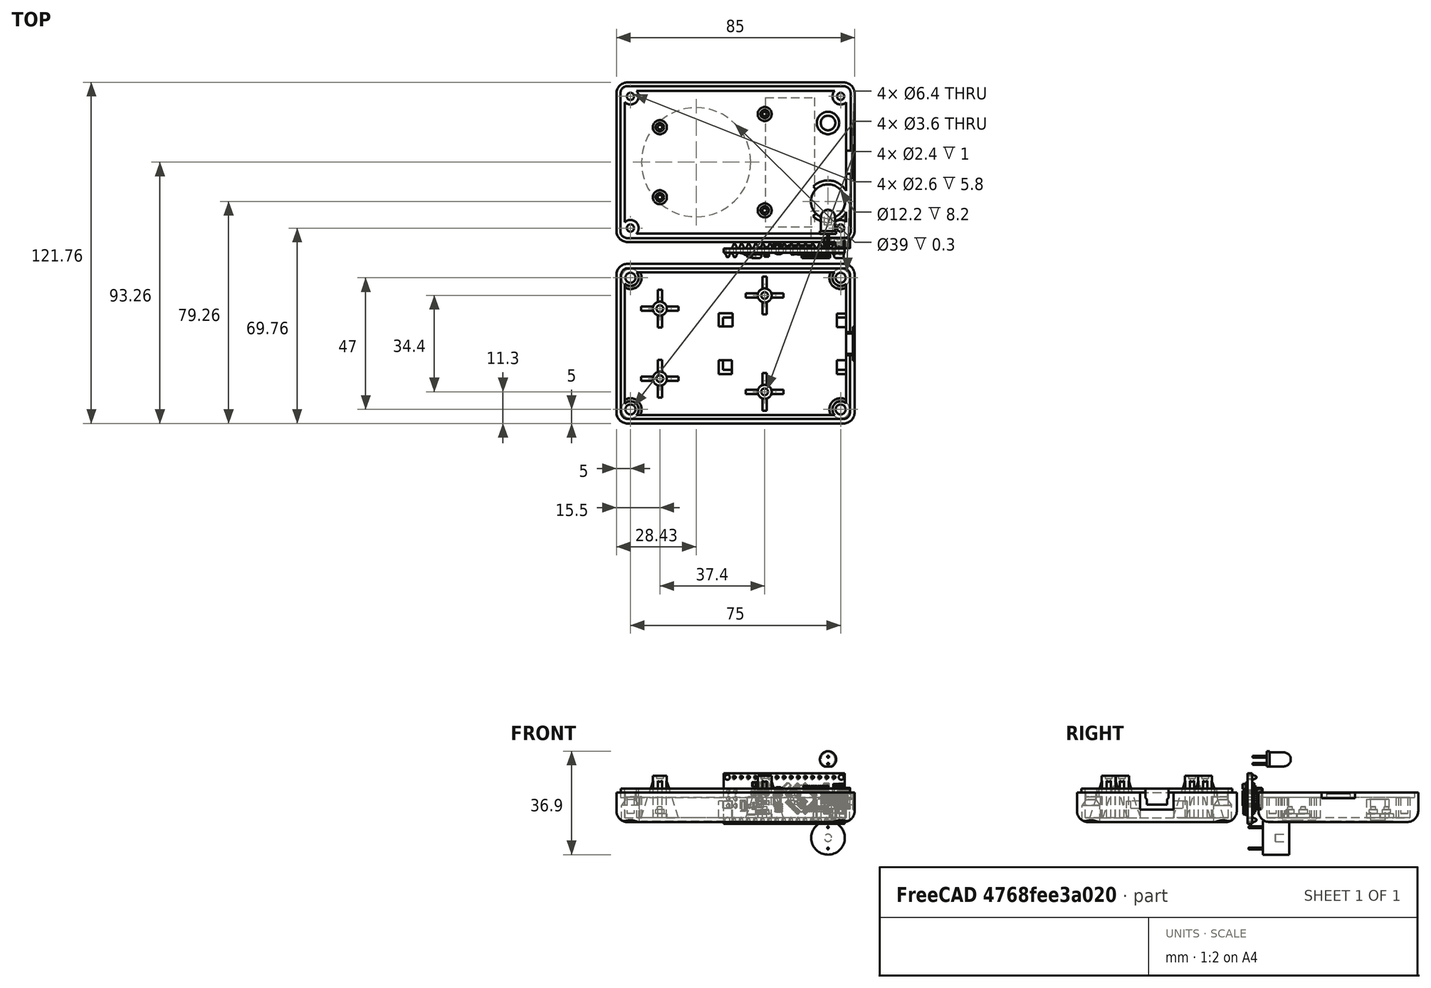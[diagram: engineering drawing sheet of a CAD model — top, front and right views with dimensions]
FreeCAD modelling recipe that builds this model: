
FCSTD DOCUMENT  (FreeCAD 0.17R13541 (Git))
Label: sportduino-master
License: All rights reserved
LicenseURL: http://en.wikipedia.org/wiki/All_rights_reserved
objects: Part::Feature×51, Part::MultiFuse×33, Part::Cylinder×24, Part::Cut×24, Part::FeaturePython×24, Part::Box×20, Part::Fillet×3, App::DocumentObjectGroup×1, Part::Sphere×1, Mesh::Feature×1, Part::Extrusion×1, Part::Cone×1
note: 182 computed .brp shape members not serialized (recipe doc carries the construction recipe); baked Part::Feature solids carry a one-line shape summary decoded from their .brp

FEATURE [Part::Feature] Part__Feature  label="User Library-arduino_nano"
  shape: bbox 43.59 x 4.635 x 18 mm, 378 faces (baked)
FEATURE [Part::Feature] Part__Feature006  label="User Library-arduino_nano006"
  Placement = pos=(23.85,1.75,-7.62) rot=(0,1,0;3.92699rad)
  shape: bbox 11.22 x 1.101 x 11.22 mm, 1866 faces (baked)
FEATURE [Part::Feature] Part__Feature007  label="User Library-arduino_nano007"
  Placement = pos=(29.05,0,-7.67) rot=(0.707107,0,-0.707107;3.14159rad)
  shape: bbox 10.2 x 1.9 x 9.71 mm, 717 faces (baked)
FEATURE [Part::Feature] Part__Feature008  label="User Library-arduino_nano008"
  Placement = pos=(21.86,0,-5.8) rot=(0.707107,0,-0.707107;3.14159rad)
  shape: bbox 3.8 x 0.6006 x 1.7 mm, 74 faces (baked)
FEATURE [Part::Feature] Part__Feature009  label="User Library-arduino_nano009"
  Placement = pos=(21.86,0,-9) rot=(0.707107,0,-0.707107;3.14159rad)
  shape: bbox 3.8 x 0.6006 x 1.7 mm, 74 faces (baked)
FEATURE [Part::Feature] Part__Feature010  label="User Library-arduino_nano010"
  Placement = pos=(36.75,0,-7.6) rot=(0.707107,0,-0.707107;3.14159rad)
  shape: bbox 3.8 x 0.6006 x 1.7 mm, 74 faces (baked)
FEATURE [Part::Feature] Part__Feature011  label="User Library-arduino_nano011"
  Placement = pos=(36.75,0,-12) rot=(0.707107,0,-0.707107;3.14159rad)
  shape: bbox 3.8 x 0.6006 x 1.7 mm, 74 faces (baked)
FEATURE [Part::Feature] Part__Feature012  label="User Library-arduino_nano012"
  Placement = pos=(8.2,0,-2.6) rot=(0.707107,0,-0.707107;3.14159rad)
  shape: bbox 3.8 x 0.6006 x 1.7 mm, 74 faces (baked)
FEATURE [Part::Feature] Part__Feature013  label="User Library-arduino_nano013"
  Placement = pos=(10.4,1.6,-2.8) rot=(0,0,1;0rad)
  shape: bbox 5.556 x 0.5822 x 2.158 mm, 43 faces (baked)
FEATURE [Part::Feature] Part__Feature014  label="User Library-arduino_nano014"
  Placement = pos=(10.4,1.6,-2.8) rot=(0,0,1;0rad)
  shape: bbox 1.4 x 0.5 x 1.2 mm, 6 faces (baked)
FEATURE [Part::Feature] Part__Feature015  label="User Library-arduino_nano015"
  Placement = pos=(10.4,1.6,-5.55) rot=(0,0,1;0rad)
  shape: bbox 5.556 x 0.5822 x 2.158 mm, 43 faces (baked)
FEATURE [Part::Feature] Part__Feature016  label="User Library-arduino_nano016"
  Placement = pos=(10.4,1.6,-5.55) rot=(0,0,1;0rad)
  shape: bbox 1.4 x 0.5 x 1.2 mm, 6 faces (baked)
FEATURE [Part::Feature] Part__Feature017  label="User Library-arduino_nano017"
  Placement = pos=(10.4,1.6,-12.5) rot=(0,0,1;0rad)
  shape: bbox 5.556 x 0.5822 x 2.158 mm, 43 faces (baked)
FEATURE [Part::Feature] Part__Feature018  label="User Library-arduino_nano018"
  Placement = pos=(10.4,1.6,-12.5) rot=(0,0,1;0rad)
  shape: bbox 1.4 x 0.5 x 1.2 mm, 6 faces (baked)
FEATURE [Part::Feature] Part__Feature019  label="User Library-arduino_nano019"
  Placement = pos=(10.4,1.6,-9.05) rot=(0,0,1;0rad)
  shape: bbox 5.556 x 0.5822 x 2.158 mm, 43 faces (baked)
FEATURE [Part::Feature] Part__Feature020  label="User Library-arduino_nano020"
  Placement = pos=(10.4,1.6,-9.05) rot=(0,0,1;0rad)
  shape: bbox 1.4 x 0.5 x 1.2 mm, 6 faces (baked)
FEATURE [Part::Feature] Part__Feature021  label="User Library-arduino_nano021"
  Placement = pos=(18.5113,1.6,-3.55414) rot=(0,-1,0;0.785398rad)
  shape: bbox 3.584 x 0.8006 x 3.584 mm, 71 faces (baked)
FEATURE [Part::Feature] Part__Feature022  label="User Library-arduino_nano022"
  Placement = pos=(38.98,1.65,-7.62) rot=(0,-1,0;1.5708rad)
  shape: bbox 9.476 x 3.823 x 11.03 mm, 248 faces (baked)
FEATURE [Part::Feature] Part__Feature023  label="User Library-arduino_nano023"
  Placement = pos=(32.28,1.65,-7.62) rot=(0,1,0;1.5708rad)
  shape: bbox 8.2 x 4.5 x 7.7 mm, 127 faces (baked)
FEATURE [Part::Feature] Part__Feature024  label="User Library-arduino_nano024"
  Placement = pos=(33.28,1.65,-9.22) rot=(0,1,0;1.5708rad)
  shape: bbox 9.423 x 2.551 x 0.5011 mm, 31 faces (baked)
FEATURE [Part::Feature] Part__Feature025  label="User Library-arduino_nano025"
  Placement = pos=(33.28,1.65,-8.42) rot=(0,1,0;1.5708rad)
  shape: bbox 9.423 x 2.551 x 0.5011 mm, 31 faces (baked)
FEATURE [Part::Feature] Part__Feature026  label="User Library-arduino_nano026"
  Placement = pos=(33.28,1.65,-7.62) rot=(0,1,0;1.5708rad)
  shape: bbox 9.423 x 2.551 x 0.5011 mm, 31 faces (baked)
FEATURE [Part::Feature] Part__Feature027  label="User Library-arduino_nano027"
  Placement = pos=(33.28,1.65,-6.82) rot=(0,1,0;1.5708rad)
  shape: bbox 9.423 x 2.551 x 0.5011 mm, 31 faces (baked)
FEATURE [Part::Feature] Part__Feature028  label="User Library-arduino_nano028"
  Placement = pos=(33.28,1.65,-6.02) rot=(0,1,0;1.5708rad)
  shape: bbox 9.423 x 2.551 x 0.5011 mm, 31 faces (baked)
FEATURE [Part::Feature] Part__Feature029  label="User Library-arduino_nano029"
  Placement = pos=(37.2,0,-3.3) rot=(0.707107,0,0.707107;3.14159rad)
  shape: bbox 4 x 1.81 x 1.7 mm, 125 faces (baked)
FEATURE [Part::Feature] Part__Feature030  label="User Library-arduino_nano030"
  Placement = pos=(7.9,0,-5.6) rot=(0.707107,0,-0.707107;3.14159rad)
  shape: bbox 4 x 1.81 x 1.7 mm, 125 faces (baked)
FEATURE [Part::Feature] Part__Feature031  label="User Library-arduino_nano031"
  Placement = pos=(15.25,1.6,-8.05) rot=(0,1,0;1.5708rad)
  shape: bbox 2.8 x 2.156 x 5.2 mm, 77 faces (baked)
FEATURE [Part::Feature] Part__Feature032  label="User Library-arduino_nano032"
  Placement = pos=(15.25,3.25,-8.05) rot=(0,0,1;0rad)
  shape: bbox 3 x 1.65 x 4 mm, 72 faces (baked)
FEATURE [Part::Feature] Part__Feature033  label="User Library-arduino_nano033"
  Placement = pos=(6.1,0,-10.16) rot=(0.707107,0,-0.707107;3.14159rad)
  shape: bbox 8.3 x 1.689 x 6.5 mm, 197 faces (baked)
FEATURE [Part::Feature] Part__Feature034  label="User Library-arduino_nano034"
  Placement = pos=(11.43,0,-4.2) rot=(0.707107,0,0.707107;3.14159rad)
  shape: bbox 1.701 x 1.385 x 4.916 mm, 85 faces (baked)
FEATURE [Part::Feature] Part__Feature035  label="User Library-arduino_nano035"
  Placement = pos=(15.75,0,-10.85) rot=(0.707107,0,0.707107;3.14159rad)
  shape: bbox 1.3 x 0.3 x 3.2 mm, 21 faces (baked)
FEATURE [Part::Feature] Part__Feature036  label="User Library-arduino_nano036"
  Placement = pos=(15.75,0,-10.85) rot=(0.707107,0,0.707107;3.14159rad)
  shape: bbox 1.5 x 0.455 x 3.2 mm, 147 faces (baked)
FEATURE [Part::Feature] Part__Feature037  label="User Library-arduino_nano037"
  Placement = pos=(15.75,0,-10.85) rot=(0.707107,0,0.707107;3.14159rad)
  shape: bbox 0.8396 x 0.4235 x 0.4127 mm, 15 faces (baked)
FEATURE [Part::Feature] Part__Feature038  label="User Library-arduino_nano038"
  Placement = pos=(15.75,0,-10.85) rot=(0.707107,0,0.707107;3.14159rad)
  shape: bbox 0.8396 x 0.4235 x 0.4127 mm, 15 faces (baked)
FEATURE [Part::Feature] Part__Feature039  label="User Library-arduino_nano039"
  Placement = pos=(15.75,0,-10.85) rot=(0.707107,0,0.707107;3.14159rad)
  shape: bbox 0.8396 x 0.4235 x 0.4127 mm, 15 faces (baked)
FEATURE [Part::Feature] Part__Feature040  label="User Library-arduino_nano040"
  Placement = pos=(15.75,0,-10.85) rot=(0.707107,0,0.707107;3.14159rad)
  shape: bbox 0.8396 x 0.4235 x 0.4127 mm, 15 faces (baked)
FEATURE [Part::Feature] Part__Feature041  label="User Library-arduino_nano041"
  Placement = pos=(15.75,0,-10.85) rot=(0.707107,0,0.707107;3.14159rad)
  shape: bbox 0.8396 x 0.4235 x 0.4127 mm, 15 faces (baked)
FEATURE [Part::Feature] Part__Feature042  label="User Library-arduino_nano042"
  Placement = pos=(15.75,0,-10.85) rot=(0.707107,0,0.707107;3.14159rad)
  shape: bbox 0.8396 x 0.4235 x 0.4127 mm, 15 faces (baked)
FEATURE [Part::Feature] Part__Feature043  label="User Library-arduino_nano043"
  Placement = pos=(15.75,0,-10.85) rot=(0.707107,0,0.707107;3.14159rad)
  shape: bbox 0.8396 x 0.4235 x 0.4127 mm, 15 faces (baked)
FEATURE [Part::Feature] Part__Feature044  label="User Library-arduino_nano044"
  Placement = pos=(15.75,0,-10.85) rot=(0.707107,0,0.707107;3.14159rad)
  shape: bbox 0.8396 x 0.4235 x 0.4127 mm, 15 faces (baked)
FEATURE [Part::Feature] Part__Feature045  label="User Library-arduino_nano045"
  Placement = pos=(15.75,0,-5.2) rot=(0.707107,0,0.707107;3.14159rad)
  shape: bbox 1.3 x 0.3 x 3.2 mm, 21 faces (baked)
FEATURE [Part::Feature] Part__Feature046  label="User Library-arduino_nano046"
  Placement = pos=(15.75,0,-5.2) rot=(0.707107,0,0.707107;3.14159rad)
  shape: bbox 1.5 x 0.455 x 3.2 mm, 136 faces (baked)
FEATURE [Part::Feature] Part__Feature047  label="User Library-arduino_nano047"
  Placement = pos=(15.75,0,-5.2) rot=(0.707107,0,0.707107;3.14159rad)
  shape: bbox 0.8396 x 0.4235 x 0.4127 mm, 15 faces (baked)
FEATURE [Part::Feature] Part__Feature048  label="User Library-arduino_nano048"
  Placement = pos=(15.75,0,-5.2) rot=(0.707107,0,0.707107;3.14159rad)
  shape: bbox 0.8396 x 0.4235 x 0.4127 mm, 15 faces (baked)
FEATURE [Part::Feature] Part__Feature049  label="User Library-arduino_nano049"
  Placement = pos=(15.75,0,-5.2) rot=(0.707107,0,0.707107;3.14159rad)
  shape: bbox 0.8396 x 0.4235 x 0.4127 mm, 15 faces (baked)
FEATURE [Part::Feature] Part__Feature050  label="User Library-arduino_nano050"
  Placement = pos=(15.75,0,-5.2) rot=(0.707107,0,0.707107;3.14159rad)
  shape: bbox 0.8396 x 0.4235 x 0.4127 mm, 15 faces (baked)
FEATURE [Part::Feature] Part__Feature051  label="User Library-arduino_nano051"
  Placement = pos=(15.75,0,-5.2) rot=(0.707107,0,0.707107;3.14159rad)
  shape: bbox 0.8396 x 0.4235 x 0.4127 mm, 15 faces (baked)
FEATURE [Part::Feature] Part__Feature052  label="User Library-arduino_nano052"
  Placement = pos=(15.75,0,-5.2) rot=(0.707107,0,0.707107;3.14159rad)
  shape: bbox 0.8396 x 0.4235 x 0.4127 mm, 15 faces (baked)
FEATURE [Part::Feature] Part__Feature053  label="User Library-arduino_nano053"
  Placement = pos=(15.75,0,-5.2) rot=(0.707107,0,0.707107;3.14159rad)
  shape: bbox 0.8396 x 0.4235 x 0.4127 mm, 15 faces (baked)
FEATURE [Part::Feature] Part__Feature054  label="User Library-arduino_nano054"
  Placement = pos=(15.75,0,-5.2) rot=(0.707107,0,0.707107;3.14159rad)
  shape: bbox 0.8396 x 0.4235 x 0.4127 mm, 15 faces (baked)
FEATURE [App::DocumentObjectGroup] Group  label="arduino"
  Group = -> [Part__Feature,Part__Feature006,Part__Feature007,Part__Feature008,Part__Feature009,Part__Feature010,Part__Feature011,Part__Feature012,Part__Feature013,Part__Feature014,Part__Feature015,Part__Feature016,Part__Feature017,Part__Feature018,Part__Feature019,Part__Feature020,Part__Feature021,Part__Feature022,Part__Feature023,Part__Feature024,Part__Feature025,Part__Feature026,Part__Feature027,+27 more]
FEATURE [Part::Cylinder] Cylinder  label="buz-cyl"
  Angle = 360
  AttacherType = Attacher::AttachEngine3D
  Height = 9.5
  Radius = 6
FEATURE [Part::Cylinder] Cylinder001  label="buz-hole"
  Angle = 360
  AttacherType = Attacher::AttachEngine3D
  Height = 5
  Placement = pos=(0,0,4.5) rot=(0,0,1;0rad)
  Radius = 1.3
FEATURE [Part::Cut] Cut
  Base = -> Cylinder
  Refine = true
  Tool = -> Cylinder001
FEATURE [Part::Cylinder] Cylinder002  label="buz-pin1"
  Angle = 360
  AttacherType = Attacher::AttachEngine3D
  Height = 5
  Placement = pos=(0,-3.8,-5) rot=(0,0,1;0rad)
  Radius = 0.3
FEATURE [Part::Cylinder] Cylinder003  label="buz-pin2"
  Angle = 360
  AttacherType = Attacher::AttachEngine3D
  Height = 5
  Placement = pos=(0,3.8,-5) rot=(0,0,1;0rad)
  Radius = 0.3
FEATURE [Part::MultiFuse] Fusion  label="Buzzer12mm"
  Placement = pos=(33.37,5.4,-21.62) rot=(-1,0,0;1.5708rad)
  Refine = true
  Shapes = -> [Cylinder003,Cylinder002,Cut]
FEATURE [Part::Cylinder] Cylinder004  label="led-cyl"
  Angle = 360
  AttacherType = Attacher::AttachEngine3D
  Height = 6.1
  Radius = 2.5
FEATURE [Part::Sphere] Sphere  label="led-sphere"
  Angle1 = -90
  Angle2 = 90
  Angle3 = 360
  AttacherType = Attacher::AttachEngine3D
  Placement = pos=(0,0,6.1) rot=(0,0,1;0rad)
  Radius = 2.5
FEATURE [Part::Cylinder] Cylinder005  label="led-cyl2"
  Angle = 360
  AttacherType = Attacher::AttachEngine3D
  Height = 1
  Radius = 2.9
FEATURE [Part::Box] Box  label="led-key-cut"
  AttacherType = Attacher::AttachEngine3D
  Height = 10
  Length = 10
  Placement = pos=(-5,2.5,0) rot=(0,0,1;0rad)
  Width = 10
FEATURE [Part::Cut] Cut001
  Base = -> Cylinder005
  Refine = true
  Tool = -> Box
FEATURE [Part::MultiFuse] Fusion001  label="led-without-pins"
  Refine = true
  Shapes = -> [Sphere,Cylinder004,Cut001]
FEATURE [Part::Box] Box001  label="led-pin1"
  AttacherType = Attacher::AttachEngine3D
  Height = 5
  Length = 0.6
  Placement = pos=(-0.3,1.27,-5) rot=(0,0,1;0rad)
  Width = 0.6
FEATURE [Part::Box] Box002  label="led-pin2"
  AttacherType = Attacher::AttachEngine3D
  Height = 5
  Length = 0.6
  Placement = pos=(-0.3,-1.27,-5) rot=(0,0,1;0rad)
  Width = 0.6
FEATURE [Part::MultiFuse] Fusion002  label="Led5mm"
  Placement = pos=(33.37,6.8,6.38) rot=(-1,0,0;1.5708rad)
  Refine = true
  Shapes = -> [Fusion001,Box001,Box002]
FEATURE [Mesh::Feature] rc  label="RC522"
  Placement = pos=(-4,72.4,-3.964) rot=(0.57735,0.57735,-0.57735;2.0944rad)
FEATURE [Part::Cylinder] Cylinder008  label="buz-holder-cyl"
  Angle = 360
  AttacherType = Attacher::AttachEngine3D
  Height = 7.4
  Placement = pos=(33.37,7.2,-21.62) rot=(-1,0,0;1.5708rad)
  Radius = 7.5
FEATURE [Part::Cylinder] Cylinder009  label="led-holder-cyl"
  Angle = 360
  AttacherType = Attacher::AttachEngine3D
  Height = 7.6
  Placement = pos=(33.37,7.8,6.38) rot=(-1,0,0;1.5708rad)
  Radius = 4
FEATURE [Part::Cylinder] Cylinder015  label="rc522-col-cyl1"
  Angle = 360
  AttacherType = Attacher::AttachEngine3D
  Height = 15.1
  Placement = pos=(10.77,-3.6,-24.82) rot=(-1,0,0;1.5708rad)
  Radius = 2.5
FEATURE [Part::Feature] Face
  shape: bbox 8.3 x 4.5 x 2e-07 mm, 1 faces, 0 solids (baked)
FEATURE [Part::Extrusion] Extrude  label="cut-mini-usb"
  Base = -> Face
  Dir = (0,0,10)
  DirMode = 0
  FaceMakerClass = Part::FaceMakerExtrusion
  LengthFwd = 0
  LengthRev = 0
  Placement = pos=(35,-4.55,42.23) rot=(0,1,0;1.5708rad)
  Solid = true
  Symmetric = false
FEATURE [Part::Box] Box005  label="middle-box"
  AttacherType = Attacher::AttachEngine3D
  Height = 53.8
  Length = 81.8
  Placement = pos=(41.27,5.5,19.28) rot=(0,1,0;3.14159rad)
  Width = 1.5
FEATURE [Part::Box] Box006  label="outer-box"
  AttacherType = Attacher::AttachEngine3D
  Height = 57
  Length = 85
  Placement = pos=(42.87,-5,20.88) rot=(0,1,0;3.14159rad)
  Width = 21
FEATURE [Part::Cylinder] Cylinder016  label="cut-antenna"
  Angle = 360
  AttacherType = Attacher::AttachEngine3D
  Height = 1
  Placement = pos=(-13.7,15.7,-7.62) rot=(-1,0,0;1.5708rad)
  Radius = 19.5
FEATURE [Part::Cylinder] Cylinder017  label="bot-corner-cyl1"
  Angle = 360
  AttacherType = Attacher::AttachEngine3D
  Height = 10.5
  Placement = pos=(37.87,-3.5,-31.12) rot=(-1,0,0;1.5708rad)
  Radius = 2.9
FEATURE [Part::Cone] Cone
  Angle = 360
  AttacherType = Attacher::AttachEngine3D
  Height = 2
  Radius1 = 3.2
  Radius2 = 1.8
FEATURE [Part::Cylinder] Cylinder018  label="Cylinder007"
  Angle = 360
  AttacherType = Attacher::AttachEngine3D
  Height = 4
  Placement = pos=(0,0,2) rot=(0,0,1;0rad)
  Radius = 1.8
FEATURE [Part::Cylinder] Cylinder019  label="Cylinder008"
  Angle = 360
  AttacherType = Attacher::AttachEngine3D
  Height = 8
  Placement = pos=(0,0,6) rot=(0,0,1;0rad)
  Radius = 1
FEATURE [Part::Cylinder] Cylinder020  label="Cylinder009"
  Angle = 360
  AttacherType = Attacher::AttachEngine3D
  Height = 20
  Placement = pos=(0,0,-20) rot=(0,0,1;0rad)
  Radius = 3.2
FEATURE [Part::MultiFuse] Fusion004  label="cut-for-screw"
  Placement = pos=(37.87,1,-31.12) rot=(-1,0,0;1.5708rad)
  Refine = true
  Shapes = -> [Cone,Cylinder018,Cylinder019,Cylinder020]
FEATURE [Part::Box] Box007  label="cut-sticker"
  AttacherType = Attacher::AttachEngine3D
  Height = 46
  Length = 17.5
  Placement = pos=(11,15.7,-30.62) rot=(0,0,1;0rad)
  Width = 1
FEATURE [Part::Box] Box008  label="inner-box"
  AttacherType = Attacher::AttachEngine3D
  Height = 51
  Length = 79
  Placement = pos=(39.87,-3.5,17.88) rot=(0,1,0;3.14159rad)
  Width = 18
FEATURE [Part::Fillet] Fillet  label="outer-box-fillet"
  Base = -> Box006
  Edges = 12 edges r=4: [Edge1,Edge2,Edge3,Edge4,Edge5,Edge6,Edge7,Edge8,Edge9,Edge10,Edge11,Edge12]
FEATURE [Part::Fillet] Fillet001  label="middle-box-fillet"
  Base = -> Box005
  Edges = 4 edges r=2.5: [Edge2,Edge4,Edge6,Edge8]
FEATURE [Part::Cylinder] Cylinder021  label="cut-buz-cyl"
  Angle = 360
  AttacherType = Attacher::AttachEngine3D
  Height = 10
  Placement = pos=(33.37,5.4,-21.62) rot=(-1,0,0;1.5708rad)
  Radius = 6.1
FEATURE [Part::Cylinder] Cylinder022  label="cut-led-cyl"
  Angle = 360
  AttacherType = Attacher::AttachEngine3D
  Height = 7.6
  Placement = pos=(33.37,7.8,6.38) rot=(-1,0,0;1.5708rad)
  Radius = 2.6
FEATURE [Part::Box] Box009  label="cut-top-cover"
  AttacherType = Attacher::AttachEngine3D
  Height = 57
  Length = 85
  Placement = pos=(42.87,5.5,20.88) rot=(0,1,0;3.14159rad)
  Width = 21
FEATURE [Part::Box] Box010  label="cut-bot-cover"
  AttacherType = Attacher::AttachEngine3D
  Height = 57
  Length = 85
  Placement = pos=(42.87,-15.5,20.88) rot=(0,1,0;3.14159rad)
  Width = 21
FEATURE [Part::Cut] Cut005
  Base = -> Fillet
  Refine = true
  Tool = -> Box009
FEATURE [Part::FeaturePython] Clone012  label="Clone of inner-box"  # Draft clone (typed FeaturePython)
  Objects = -> [Box008]
  Placement = pos=(39.87,-3.5,17.88) rot=(0,1,0;3.14159rad)
  Scale = (1,1,1)
FEATURE [Part::FeaturePython] Clone013  label="Clone of outer-box-fillet"  # Draft clone (typed FeaturePython)
  Objects = -> [Fillet]
  Scale = (1,1,1)
FEATURE [Part::MultiFuse] Fusion005
  Refine = true
  Shapes = -> [Cut005,Fillet001]
FEATURE [Part::Cut] Cut006
  Base = -> Fusion005
  Refine = true
  Tool = -> Box008
FEATURE [Part::Box] Box011  label="add-cut-mini-usb"
  AttacherType = Attacher::AttachEngine3D
  Height = 8.3
  Length = 10
  Placement = pos=(38,4,-11.77) rot=(0,0,1;0rad)
  Width = 10
FEATURE [Part::Cylinder] Cylinder023  label="bot-corner-cyl2"
  Angle = 360
  AttacherType = Attacher::AttachEngine3D
  Height = 7.6
  Placement = pos=(37.87,-3.6,-31.12) rot=(-1,0,0;1.5708rad)
  Radius = 4
FEATURE [Part::MultiFuse] Fusion006  label="bot-curner-col1"
  Refine = true
  Shapes = -> [Cylinder017,Cylinder023]
FEATURE [Part::FeaturePython] Clone014  label="bot-curner-col2"  # Draft clone (typed FeaturePython)
  Objects = -> [Fusion006]
  Placement = pos=(0,0,47) rot=(0,0,1;0rad)
  Scale = (1,1,1)
FEATURE [Part::FeaturePython] Clone015  label="bot-curner-col3"  # Draft clone (typed FeaturePython)
  Objects = -> [Fusion006]
  Placement = pos=(-75,0,0) rot=(0,0,1;0rad)
  Scale = (1,1,1)
FEATURE [Part::FeaturePython] Clone016  label="bot-curner-col4"  # Draft clone (typed FeaturePython)
  Objects = -> [Fusion006]
  Placement = pos=(-75,0,47) rot=(0,0,1;0rad)
  Scale = (1,1,1)
FEATURE [Part::FeaturePython] Clone017  label="cut-for-screw2"  # Draft clone (typed FeaturePython)
  Objects = -> [Fusion004]
  Placement = pos=(37.87,1,15.88) rot=(-1,0,0;1.5708rad)
  Scale = (1,1,1)
FEATURE [Part::FeaturePython] Clone018  label="cut-for-screw3"  # Draft clone (typed FeaturePython)
  Objects = -> [Fusion004]
  Placement = pos=(-37.13,1,-31.12) rot=(-1,0,0;1.5708rad)
  Scale = (1,1,1)
FEATURE [Part::FeaturePython] Clone019  label="cut-for-screw4"  # Draft clone (typed FeaturePython)
  Objects = -> [Fusion004]
  Placement = pos=(-37.13,1,15.88) rot=(-1,0,0;1.5708rad)
  Scale = (1,1,1)
FEATURE [Part::Cylinder] Cylinder027  label="rc522-col-hole"
  Angle = 360
  AttacherType = Attacher::AttachEngine3D
  Height = 1
  Placement = pos=(10.77,11.5,-24.82) rot=(1,0,0;1.5708rad)
  Radius = 1.2
FEATURE [Part::Box] Box012  label="cut-usb-cable"
  AttacherType = Attacher::AttachEngine3D
  Height = 12
  Length = 10
  Placement = pos=(42.27,-0.55,-13.62) rot=(0,0,1;0rad)
  Width = 8
FEATURE [Part::FeaturePython] Clone023  label="Clone of cut-usb-cable"  # Draft clone (typed FeaturePython)
  Objects = -> [Box012]
  Placement = pos=(42.27,-0.55,-13.62) rot=(0,0,1;0rad)
  Scale = (1,1,1)
FEATURE [Part::FeaturePython] Clone025  label="Clone of cut-mini-usb"  # Draft clone (typed FeaturePython)
  Objects = -> [Extrude]
  Placement = pos=(35,-4.55,42.23) rot=(0,1,0;1.5708rad)
  Scale = (1,1,1)
FEATURE [Part::Cut] Cut016
  Base = -> Clone013
  Refine = true
  Tool = -> Box010
FEATURE [Part::Cut] Cut017
  Base = -> Cut016
  Refine = true
  Tool = -> Clone012
FEATURE [Part::Cylinder] Cylinder028  label="top-corner-cyl"
  Angle = 360
  AttacherType = Attacher::AttachEngine3D
  Height = 7.5
  Placement = pos=(37.87,7.2,-31.12) rot=(-1,0,0;1.5708rad)
  Radius = 2.9
FEATURE [Part::Cylinder] Cylinder031  label="top-corner-hole"
  Angle = 360
  AttacherType = Attacher::AttachEngine3D
  Height = 6
  Placement = pos=(37.87,7,-31.12) rot=(-1,0,0;1.5708rad)
  Radius = 1.3
FEATURE [Part::Cut] Cut019  label="top-corner-col1"
  Base = -> Cylinder028
  Refine = true
  Tool = -> Cylinder031
FEATURE [Part::FeaturePython] Clone027  label="top-corner-col2"  # Draft clone (typed FeaturePython)
  Objects = -> [Cut019]
  Placement = pos=(0,0,47) rot=(0,0,1;0rad)
  Scale = (1,1,1)
FEATURE [Part::FeaturePython] Clone028  label="top-corner-col3"  # Draft clone (typed FeaturePython)
  Objects = -> [Cut019]
  Placement = pos=(-75,0,0) rot=(0,0,1;0rad)
  Scale = (1,1,1)
FEATURE [Part::FeaturePython] Clone029  label="top-corner-col4"  # Draft clone (typed FeaturePython)
  Objects = -> [Cut019]
  Placement = pos=(-75,0,47) rot=(0,0,1;0rad)
  Scale = (1,1,1)
FEATURE [Part::Box] Box013  label="add-mini-usb-wall"
  AttacherType = Attacher::AttachEngine3D
  Height = 8.3
  Length = 1.6
  Placement = pos=(39.87,5.5,-11.77) rot=(0,0,1;0rad)
  Width = 1.7
FEATURE [Part::Cylinder] Cylinder032  label="rc522-top-col-cyl1"
  Angle = 360
  AttacherType = Attacher::AttachEngine3D
  Height = 2.4
  Placement = pos=(10.77,13.1,-24.82) rot=(-1,0,0;1.5708rad)
  Radius = 2.5
FEATURE [Part::Cylinder] Cylinder033  label="rc522-top-col-cyl2"
  Angle = 360
  AttacherType = Attacher::AttachEngine3D
  Height = 1.5
  Placement = pos=(10.77,13,-24.82) rot=(1,0,0;1.5708rad)
  Radius = 1.5
FEATURE [Part::Cylinder] Cylinder034  label="rc522-top-col-cyl3"
  Angle = 360
  AttacherType = Attacher::AttachEngine3D
  Height = 1
  Placement = pos=(10.77,11.5,-24.82) rot=(1,0,0;1.5708rad)
  Radius = 0.8
FEATURE [Part::MultiFuse] Fusion026  label="rc522-top-col1"
  Refine = true
  Shapes = -> [Cylinder032,Cylinder033,Cylinder034]
FEATURE [Part::FeaturePython] Clone030  label="rc522-top-col2"  # Draft clone (typed FeaturePython)
  Objects = -> [Fusion026]
  Placement = pos=(0,0,34.4) rot=(0,0,1;0rad)
  Scale = (1,1,1)
FEATURE [Part::FeaturePython] Clone031  label="rc522-top-col3"  # Draft clone (typed FeaturePython)
  Objects = -> [Fusion026]
  Placement = pos=(-37.4,0,4.7) rot=(0,0,1;0rad)
  Scale = (1,1,1)
FEATURE [Part::FeaturePython] Clone032  label="rc522-top-col4"  # Draft clone (typed FeaturePython)
  Objects = -> [Fusion026]
  Placement = pos=(-37.4,0,29.7) rot=(0,0,1;0rad)
  Scale = (1,1,1)
FEATURE [Part::Cylinder] Cylinder035  label="cut-buz-cyl2"
  Angle = 90
  AttacherType = Attacher::AttachEngine3D
  Height = 10.5
  Placement = pos=(33.37,4.4,-21.62) rot=(-0.279553,0.678915,0.678915;2.59356rad)
  Radius = 8
FEATURE [Part::Box] Box014  label="Cube"
  AttacherType = Attacher::AttachEngine3D
  Height = 4.9
  Length = 4.7
  Placement = pos=(36.5,-3.6,-1.7) rot=(0,0,1;0rad)
  Width = 3.6
FEATURE [Part::Box] Box015  label="Cube001"
  AttacherType = Attacher::AttachEngine3D
  Height = 1.5
  Length = 4.7
  Placement = pos=(36.5,-3.6,1.7) rot=(0,0,1;0rad)
  Width = 6.1
FEATURE [Part::MultiFuse] Fusion037  label="arduino-cube-col1"
  Refine = true
  Shapes = -> [Box015,Box014]
FEATURE [Part::FeaturePython] Clone035  label="arduino-cube-col2"  # Draft clone (typed FeaturePython)
  Objects = -> [Fusion037]
  Placement = pos=(77.7,0,-15.2) rot=(0,1,0;3.14159rad)
  Scale = (1,1,1)
FEATURE [Part::Box] Box016  label="Cube002"
  AttacherType = Attacher::AttachEngine3D
  Height = 1.5
  Length = 4.67
  Placement = pos=(-5.62,-3.6,1.7) rot=(0,0,1;0rad)
  Width = 6.1
FEATURE [Part::Box] Box017  label="Cube003"
  AttacherType = Attacher::AttachEngine3D
  Height = 3.4
  Length = 3.17
  Placement = pos=(-0.95,-3.6,1.7) rot=(0,1,0;3.14159rad)
  Width = 3.6
FEATURE [Part::Box] Box018  label="Cube004"
  AttacherType = Attacher::AttachEngine3D
  Height = 4.9
  Length = 1.5
  Placement = pos=(-5.62,-3.6,-1.7) rot=(0,0,1;0rad)
  Width = 6.1
FEATURE [Part::MultiFuse] Fusion038  label="arduino-cube-col3"
  Refine = true
  Shapes = -> [Box018,Box017,Box016]
FEATURE [Part::FeaturePython] Clone036  label="arduino-cube-col4"  # Draft clone (typed FeaturePython)
  Objects = -> [Fusion038]
  Placement = pos=(-2.42,0,-12.82) rot=(0,-1,0;1.5708rad)
  Scale = (1,1,1)
FEATURE [Part::Box] Box019  label="Cube005"
  AttacherType = Attacher::AttachEngine3D
  Height = 1.5
  Length = 5
  Placement = pos=(12.5,-3.6,-25.57) rot=(0,0,1;0rad)
  Width = 15.1
FEATURE [Part::Box] Box020  label="Cube006"
  AttacherType = Attacher::AttachEngine3D
  Height = 1.5
  Length = 5
  Placement = pos=(17.5,-3.6,-25.57) rot=(0,0,1;0.314159rad)
  Width = 18
FEATURE [Part::Cut] Cut027
  Base = -> Box019
  Refine = true
  Tool = -> Box020
FEATURE [Part::FeaturePython] Array  # Draft array (typed FeaturePython)
  Angle = 360
  ArrayType = 1
  Axis = (0,1,0)
  Base = -> Cut027
  Center = (10.77,0,-24.82)
  Fuse = false
  IntervalAxis = (0,0,0)
  IntervalX = (1,0,0)
  IntervalY = (0,1,0)
  IntervalZ = (0,0,0)
  NumberPolar = 4
  NumberX = 2
  NumberY = 2
  NumberZ = 1
FEATURE [Part::MultiFuse] Fusion039
  Refine = true
  Shapes = -> [Cylinder015,Array]
FEATURE [Part::Cut] Cut028  label="rc522-col1"
  Base = -> Fusion039
  Refine = true
  Tool = -> Cylinder027
FEATURE [Part::FeaturePython] Clone037  label="rc522-col2"  # Draft clone (typed FeaturePython)
  Objects = -> [Cut028]
  Placement = pos=(0,0,34.4) rot=(0,0,1;0rad)
  Scale = (1,1,1)
FEATURE [Part::FeaturePython] Clone038  label="rc522-col3"  # Draft clone (typed FeaturePython)
  Objects = -> [Cut028]
  Placement = pos=(-37.4,0,4.7) rot=(0,0,1;0rad)
  Scale = (1,1,1)
FEATURE [Part::FeaturePython] Clone039  label="rc522-col4"  # Draft clone (typed FeaturePython)
  Objects = -> [Cut028]
  Placement = pos=(-37.4,0,29.7) rot=(0,0,1;0rad)
  Scale = (1,1,1)
FEATURE [Part::Box] Box021  label="top-middle-box"
  AttacherType = Attacher::AttachEngine3D
  Height = 54.2
  Length = 82.2
  Placement = pos=(41.47,5.5,19.48) rot=(0,1,0;3.14159rad)
  Width = 1.7
FEATURE [Part::Fillet] Fillet002  label="top-middle-box-fillet"
  Base = -> Box021
  Edges = 4 edges r=2.5: [Edge2,Edge4,Edge6,Edge8]
FEATURE [Part::Cut] Cut033
  Base = -> Cut017
  Refine = true
  Tool = -> Fillet002
FEATURE [Part::Cut] Cut038
  Base = -> Cylinder008
  Refine = true
  Tool = -> Cylinder035
FEATURE [Part::Cut] Cut045
  Base = -> Cut006
  Refine = true
  Tool = -> Extrude
FEATURE [Part::Cut] Cut046
  Base = -> Cut045
  Refine = true
  Tool = -> Box011
FEATURE [Part::Cut] Cut047
  Base = -> Cut046
  Refine = true
  Tool = -> Box012
FEATURE [Part::MultiFuse] Fusion063
  Refine = true
  Shapes = -> [Cut047,Fusion006]
FEATURE [Part::MultiFuse] Fusion064
  Refine = true
  Shapes = -> [Fusion063,Clone014]
FEATURE [Part::MultiFuse] Fusion065
  Refine = true
  Shapes = -> [Fusion064,Clone015]
FEATURE [Part::MultiFuse] Fusion066
  Refine = true
  Shapes = -> [Fusion065,Clone016]
FEATURE [Part::Cut] Cut048
  Base = -> Fusion066
  Refine = true
  Tool = -> Fusion004
FEATURE [Part::Cut] Cut049
  Base = -> Cut048
  Refine = true
  Tool = -> Clone017
FEATURE [Part::Cut] Cut050
  Base = -> Cut049
  Refine = true
  Tool = -> Clone018
FEATURE [Part::Cut] Cut051
  Base = -> Cut050
  Refine = true
  Tool = -> Clone019
FEATURE [Part::MultiFuse] Fusion067
  Refine = true
  Shapes = -> [Cut051,Cut028]
FEATURE [Part::MultiFuse] Fusion068
  Refine = true
  Shapes = -> [Fusion067,Clone037]
FEATURE [Part::MultiFuse] Fusion069
  Refine = true
  Shapes = -> [Fusion068,Clone038]
FEATURE [Part::MultiFuse] Fusion070
  Refine = true
  Shapes = -> [Fusion069,Clone039]
FEATURE [Part::MultiFuse] Fusion071
  Refine = true
  Shapes = -> [Fusion070,Fusion037]
FEATURE [Part::MultiFuse] Fusion072
  Refine = true
  Shapes = -> [Fusion071,Clone035]
FEATURE [Part::MultiFuse] Fusion073
  Refine = true
  Shapes = -> [Fusion072,Fusion038]
FEATURE [Part::MultiFuse] Fusion074  label="bottom-lid-release"
  Refine = true
  Shapes = -> [Fusion073,Clone036]
FEATURE [Part::MultiFuse] Fusion075
  Refine = true
  Shapes = -> [Cut033,Box013]
FEATURE [Part::Cut] Cut052
  Base = -> Fusion075
  Refine = true
  Tool = -> Clone025
FEATURE [Part::Cut] Cut053
  Base = -> Cut052
  Refine = true
  Tool = -> Clone023
FEATURE [Part::Cut] Cut054
  Base = -> Cut053
  Refine = true
  Tool = -> Box007
FEATURE [Part::Cut] Cut055
  Base = -> Cut054
  Refine = true
  Tool = -> Cylinder016
FEATURE [Part::MultiFuse] Fusion076
  Refine = true
  Shapes = -> [Cut055,Cut019]
FEATURE [Part::MultiFuse] Fusion077
  Refine = true
  Shapes = -> [Fusion076,Clone027]
FEATURE [Part::MultiFuse] Fusion078
  Refine = true
  Shapes = -> [Fusion077,Clone028]
FEATURE [Part::MultiFuse] Fusion079
  Refine = true
  Shapes = -> [Fusion078,Clone029]
FEATURE [Part::MultiFuse] Fusion080
  Refine = true
  Shapes = -> [Fusion079,Fusion026]
FEATURE [Part::MultiFuse] Fusion081
  Refine = true
  Shapes = -> [Fusion080,Clone030]
FEATURE [Part::MultiFuse] Fusion082
  Refine = true
  Shapes = -> [Fusion081,Clone031]
FEATURE [Part::MultiFuse] Fusion083
  Refine = true
  Shapes = -> [Fusion082,Clone032]
FEATURE [Part::MultiFuse] Fusion084
  Refine = true
  Shapes = -> [Fusion083,Cut038]
FEATURE [Part::MultiFuse] Fusion085
  Refine = true
  Shapes = -> [Fusion084,Cylinder009]
FEATURE [Part::Cut] Cut056
  Base = -> Fusion085
  Refine = true
  Tool = -> Cylinder022
FEATURE [Part::Cut] Cut057  label="top-lid-release"
  Base = -> Cut056
  Refine = true
  Tool = -> Cylinder021
FEATURE [Part::FeaturePython] Clone040  label="bottom-lid-print"  # Draft clone (typed FeaturePython)
  Objects = -> [Fusion074]
  Placement = pos=(0,-40,-11) rot=(1,0,0;1.5708rad)
  Scale = (1,1,1)
FEATURE [Part::FeaturePython] Clone041  label="top-lid-print"  # Draft clone (typed FeaturePython)
  Objects = -> [Cut057]
  Placement = pos=(0,40,0) rot=(-1,0,0;1.5708rad)
  Scale = (1,1,1)
